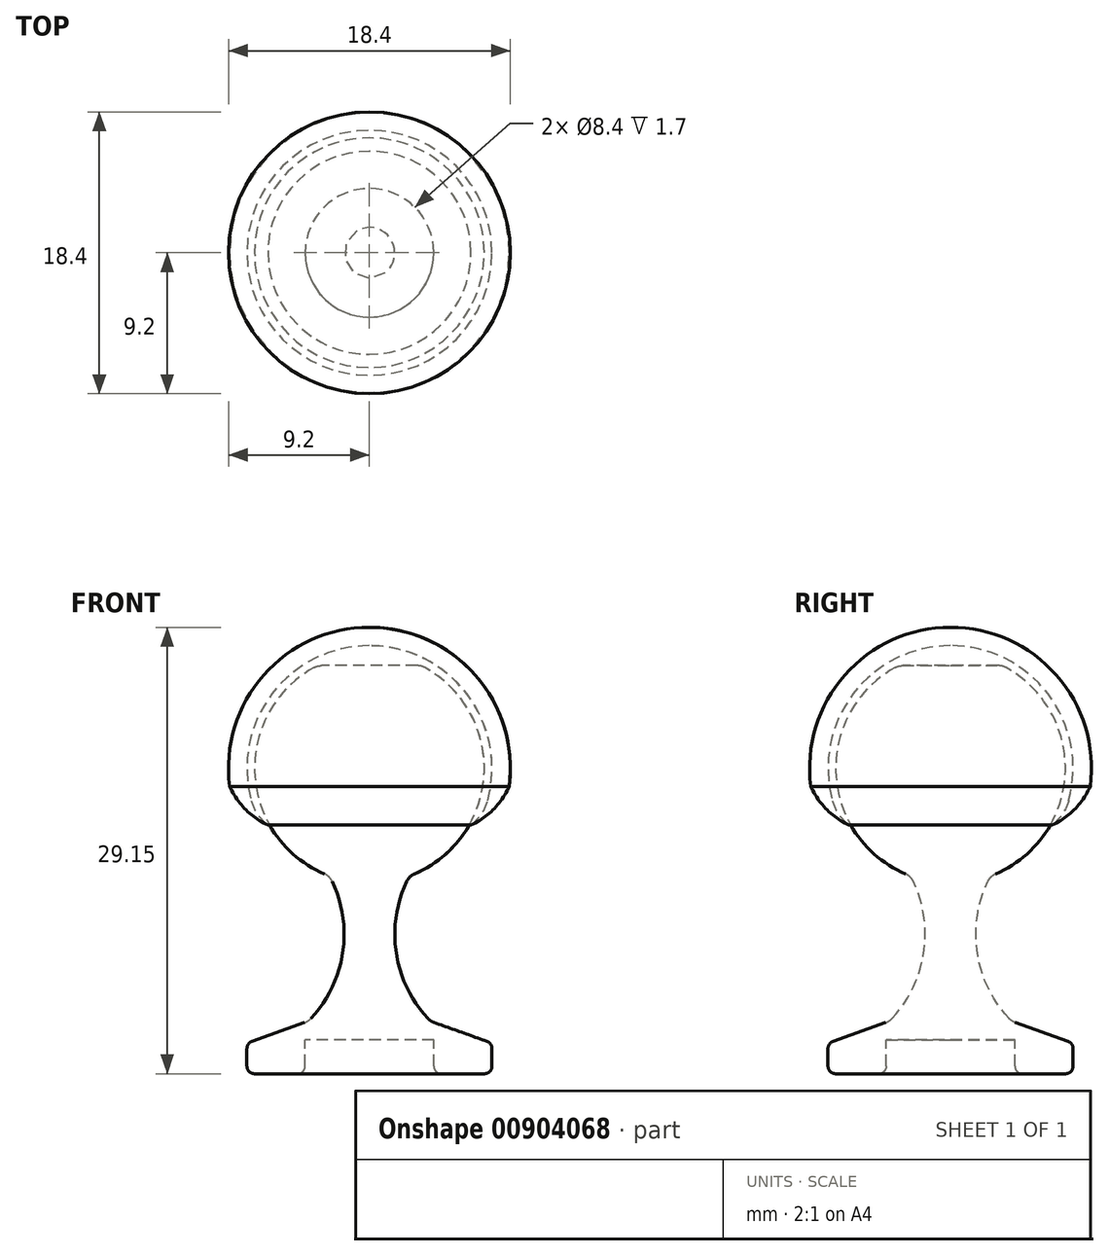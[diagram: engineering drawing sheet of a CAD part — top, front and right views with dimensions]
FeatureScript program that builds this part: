
annotation { "Feature Type Name" : "Feature", "Feature Type Description" : "" }
export const myFeature = defineFeature(function(context is Context, id is Id, definition is map)
    precondition{}
    {
        {
            var Q0;
            Q0=qCreatedBy(makeId("Front.planeOp"),FACE);
            var sketch = newSketch(context, id + "F0", { "sketchPlane" : qUnion([Q0])});
            skArc(sketch, "E0", {"start": v(2.94, 13.05) * mm, "mid": v(7.5, 19.58) * mm, "end": v(3.61, 26.52) * mm});
            skArc(sketch, "E1", {"start": v(7.72, 17.84) * mm, "mid": v(6.36, 24.8) * mm, "end": v(0, 27.95) * mm});
            skArc(sketch, "E2", {"start": v(9.12, 18.77) * mm, "mid": v(6.91, 26.02) * mm, "end": v(0, 29.15) * mm});
            skLineSegment(sketch, "E3", {"start": v(0, 26.65) * mm, "end": v(3.13, 26.65) * mm});
            skPoint(sketch, "E4.orphan", {"position": v(0.63, 27.42) * mm});
            skPoint(sketch, "E5.visualSharp", {"position": v(3.38, 26.65) * mm});
            skArc(sketch, "E5.filletArc", {"start": v(3.61, 26.52) * mm, "mid": v(3.38, 26.61) * mm, "end": v(3.13, 26.65) * mm});
            skPoint(sketch, "E6.endSnap0", {"position": v(9.2, 20.15) * mm});
            skPoint(sketch, "E7.trimOffspring.end.orphan", {"position": v(11.75, 20.15) * mm});
            skPoint(sketch, "E8.visualSharp", {"position": v(7.45, 17.03) * mm});
            skArc(sketch, "E8.filletArc", {"start": v(6.63, 16.24) * mm, "mid": v(7.3, 16.95) * mm, "end": v(7.72, 17.84) * mm});
            skLineSegment(sketch, "E9", {"start": v(4.22, 3.34) * mm, "end": v(7.67, 2.12) * mm});
            skLineSegment(sketch, "E10", {"start": v(8, 1.65) * mm, "end": v(8, 0.5) * mm});
            skLineSegment(sketch, "E11", {"start": v(7.5, 0) * mm, "end": v(4.2, 0) * mm});
            skPoint(sketch, "E12.orphan", {"position": v(4.84, 0) * mm});
            skPoint(sketch, "E13.visualSharp", {"position": v(8, 0) * mm});
            skArc(sketch, "E13.filletArc", {"start": v(7.5, 0) * mm, "mid": v(7.85, 0.15) * mm, "end": v(8, 0.5) * mm});
            skPoint(sketch, "E14.visualSharp", {"position": v(8, 2) * mm});
            skArc(sketch, "E14.filletArc", {"start": v(8, 1.65) * mm, "mid": v(7.9, 1.94) * mm, "end": v(7.67, 2.12) * mm});
            skLineSegment(sketch, "E15", {"start": v(0, 44.51) * mm, "end": v(0, 2.2) * mm});
            skLineSegment(sketch, "E16", {"start": v(4.2, 0) * mm, "end": v(4.2, 2.2) * mm});
            skLineSegment(sketch, "E17", {"start": v(4.2, 2.2) * mm, "end": v(0, 2.2) * mm});
            skArc(sketch, "E18", {"start": v(2.43, 12.56) * mm, "mid": v(1.75, 7.87) * mm, "end": v(3.83, 3.6) * mm});
            skPoint(sketch, "E19.visualSharp", {"position": v(2.62, 12.92) * mm});
            skArc(sketch, "E19.filletArc", {"start": v(2.94, 13.05) * mm, "mid": v(2.64, 12.85) * mm, "end": v(2.43, 12.56) * mm});
            skPoint(sketch, "E20.visualSharp", {"position": v(4, 3.42) * mm});
            skArc(sketch, "E20.filletArc", {"start": v(3.83, 3.6) * mm, "mid": v(4, 3.45) * mm, "end": v(4.22, 3.34) * mm});
            skPoint(sketch, "E21.orphan", {"position": v(0, 0) * mm});
            skLineSegment(sketch, "E22.trimOffspring", {"start": v(0, 0) * mm, "end": v(0, -11.97) * mm});
            skArc(sketch, "E23", {"start": v(6.63, 16.24) * mm, "mid": v(8.1, 17.27) * mm, "end": v(9.12, 18.77) * mm});
            skSolve(sketch);
        }
        {
            var Q0;
            Q0 = qSketchRegion(id + "F0", true);
            var Q1;
            Q1=sQuery(id+"F0.wireOp",EDGE,"E15");
            revolve(context, id + "F1", {"surfaceOperationType" : NewSurfaceOperationType.NEW, "entities" : qUnion([Q0]), "axis" : qUnion([Q1]), "revolveType" : RevolveType.FULL});
        }
        {
            var Q0;
            Q0=makeQuery(id+"F1.opRevolve","SWEPT_EDGE",EDGE,{"disambiguationData":[OSD([sQuery(id+"F0.wireOp",EDGE,"E11"),sQuery(id+"F0.wireOp",EDGE,"E16")])]});
            fillet(context, id + "F2", {"entities" : qUnion([Q0]), "radius" : 0.5 * mm, "tangentPropagation" : true, "allowEdgeOverflow" : false});
        }
    });
